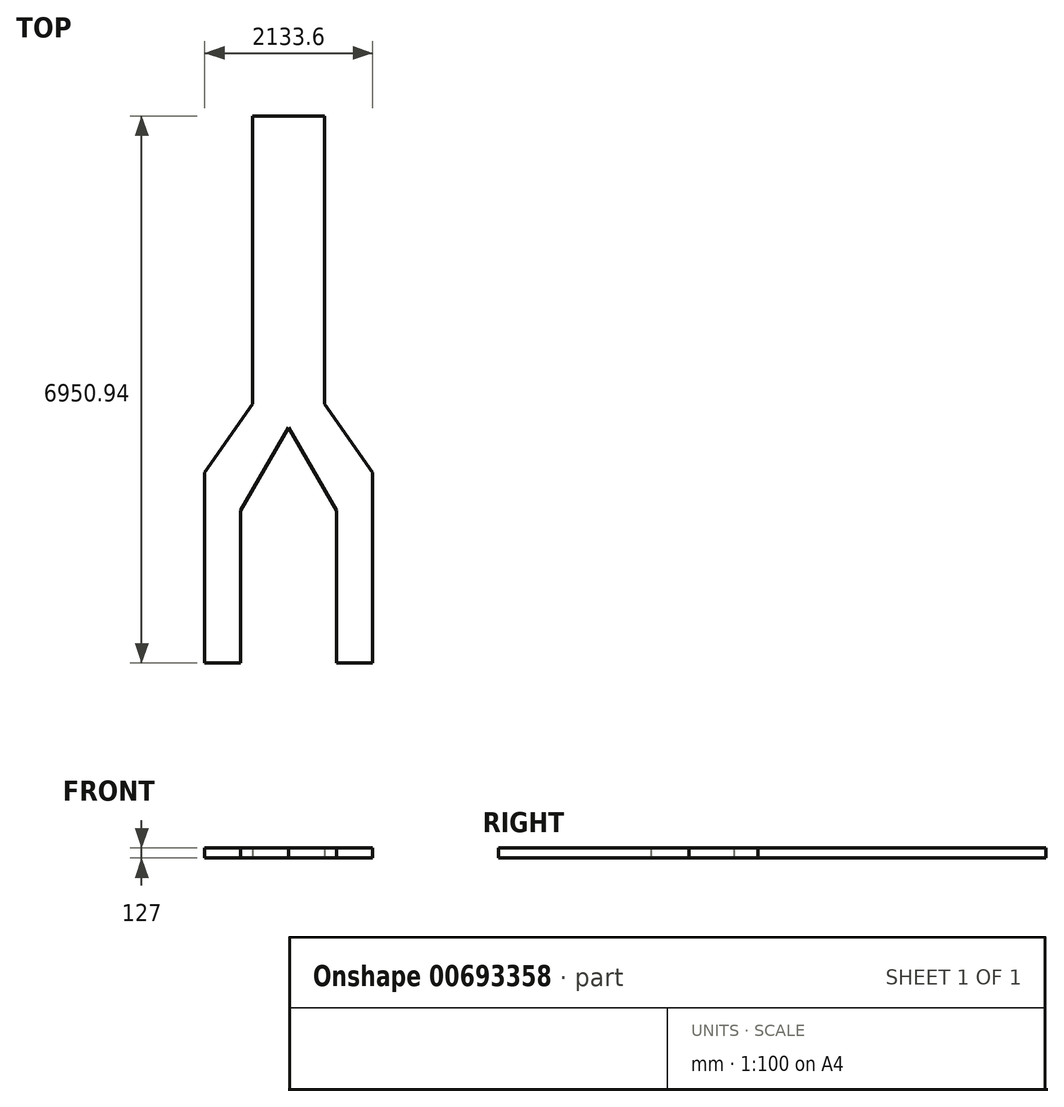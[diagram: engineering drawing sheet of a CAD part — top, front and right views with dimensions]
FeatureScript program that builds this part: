
annotation { "Feature Type Name" : "Feature", "Feature Type Description" : "" }
export const myFeature = defineFeature(function(context is Context, id is Id, definition is map)
    precondition{}
    {
        {
            var Q0;
            Q0=qCreatedBy(makeId("Top.planeOp"),FACE);
            var sketch = newSketch(context, id + "F0", { "sketchPlane" : qUnion([Q0])});
            skLineSegment(sketch, "E0.bottom", {"start": v(0, 0) * mm, "end": v(-457.2, 0) * mm});
            skLineSegment(sketch, "E0.left", {"start": v(0, 0) * mm, "end": v(0, 1934.9) * mm});
            skLineSegment(sketch, "E1", {"start": v(0, 1934.9) * mm, "end": v(609.6, 2990.76) * mm});
            skLineSegment(sketch, "E2", {"start": v(152.4, 3293.34) * mm, "end": v(-457.2, 2417.87) * mm});
            skLineSegment(sketch, "E3", {"start": v(-457.2, 2417.87) * mm, "end": v(-457.2, 0) * mm});
            skLineSegment(sketch, "E4.MirrorCS", {"start": v(1066.8, 3293.34) * mm, "end": v(1676.4, 2417.87) * mm});
            skLineSegment(sketch, "E5.MirrorCS", {"start": v(1676.4, 2417.87) * mm, "end": v(1676.4, 0) * mm});
            skLineSegment(sketch, "E6.MirrorCS", {"start": v(1219.2, 0) * mm, "end": v(1219.2, 1934.9) * mm});
            skLineSegment(sketch, "E7", {"start": v(1219.2, 0) * mm, "end": v(1676.4, 0) * mm});
            skLineSegment(sketch, "E8", {"start": v(1219.2, 1934.9) * mm, "end": v(609.6, 2990.76) * mm});
            skLineSegment(sketch, "E9.top", {"start": v(1066.8, 6950.94) * mm, "end": v(152.4, 6950.94) * mm});
            skLineSegment(sketch, "E9.left", {"start": v(1066.8, 3293.34) * mm, "end": v(1066.8, 6950.94) * mm});
            skLineSegment(sketch, "E9.right", {"start": v(152.4, 3293.34) * mm, "end": v(152.4, 6950.94) * mm});
            skSolve(sketch);
        }
        {
            var Q0;
            Q0=qSketchRegion(id+"F0",true);
            extrude(context, id + "F1", {"entities" : qUnion([Q0]), "depth" : 127 * mm, "offsetDistance" : 25.4 * mm});
        }
    });
